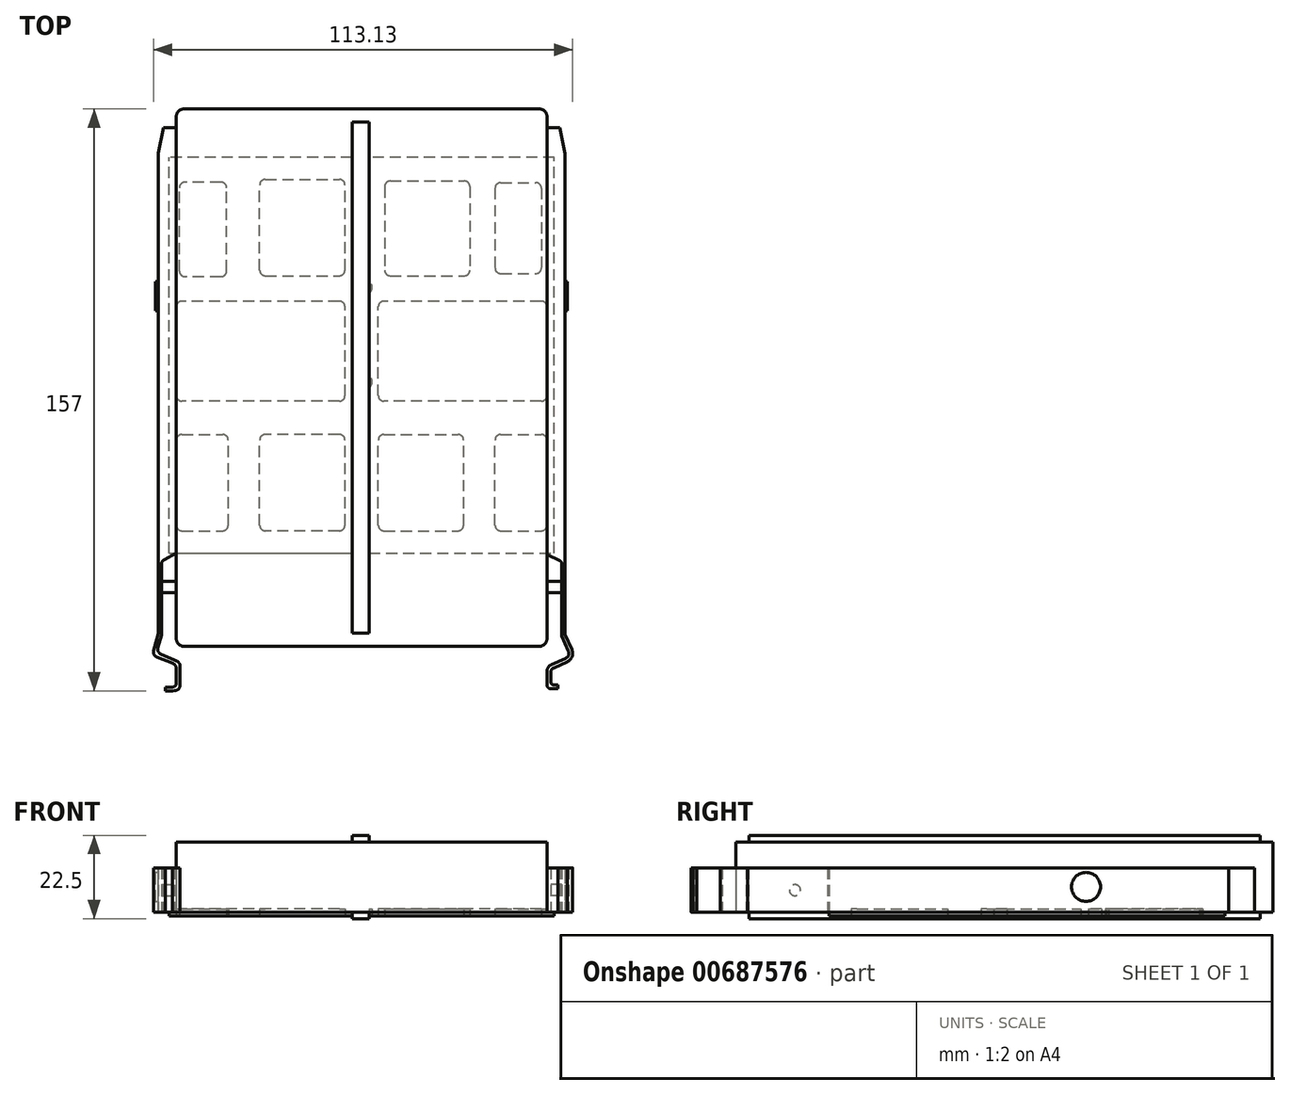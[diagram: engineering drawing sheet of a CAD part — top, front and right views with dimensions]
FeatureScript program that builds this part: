
annotation { "Feature Type Name" : "Feature", "Feature Type Description" : "" }
export const myFeature = defineFeature(function(context is Context, id is Id, definition is map)
    precondition{}
    {
        {
            var Q0;
            Q0=qCreatedBy(makeId("Top.planeOp"),FACE);
            var sketch = newSketch(context, id + "F0", { "sketchPlane" : qUnion([Q0])});
            skLineSegment(sketch, "E0", {"start": v(45.84, 65.9) * mm, "end": v(45.84, -75.1) * mm});
            skLineSegment(sketch, "E1", {"start": v(43.84, 67.9) * mm, "end": v(-52.16, 67.9) * mm});
            skLineSegment(sketch, "E2", {"start": v(-54.16, 65.9) * mm, "end": v(-54.16, -75.1) * mm});
            skLineSegment(sketch, "E3", {"start": v(-52.16, -77.1) * mm, "end": v(43.84, -77.1) * mm});
            skPoint(sketch, "E4.visualSharp", {"position": v(-54.16, 67.9) * mm});
            skArc(sketch, "E4.filletArc", {"start": v(-52.16, 67.9) * mm, "mid": v(-53.58, 67.31) * mm, "end": v(-54.16, 65.9) * mm});
            skPoint(sketch, "E5.visualSharp", {"position": v(45.84, 67.9) * mm});
            skArc(sketch, "E5.filletArc", {"start": v(45.84, 65.9) * mm, "mid": v(45.25, 67.31) * mm, "end": v(43.84, 67.9) * mm});
            skPoint(sketch, "E6.visualSharp", {"position": v(-54.16, -77.1) * mm});
            skArc(sketch, "E6.filletArc", {"start": v(-54.16, -75.1) * mm, "mid": v(-53.58, -76.52) * mm, "end": v(-52.16, -77.1) * mm});
            skPoint(sketch, "E7.visualSharp", {"position": v(45.84, -77.1) * mm});
            skArc(sketch, "E7.filletArc", {"start": v(43.84, -77.1) * mm, "mid": v(45.25, -76.52) * mm, "end": v(45.84, -75.1) * mm});
            skSolve(sketch);
        }
        {
            var Q0;
            Q0=makeQuery(id+"F0.imprint","IMPRINT",FACE,{"disambiguationData":[TD([[makeQuery(id+"F0.imprint","IMPRINT",EDGE,{"derivedFrom":sQuery(id+"F0.wireOp",EDGE,"E0")}),-1.0]])]});
            extrude(context, id + "F1", {"entities" : qUnion([Q0]), "depth" : 19 * mm, "offsetDistance" : 25 * mm});
        }
        {
            var Q0;
            Q0=makeQuery(id+"F1.opExtrude","SWEPT_FACE",FACE,{"disambiguationData":[OSD([sQuery(id+"F0.wireOp",EDGE,"E2")])]});
            var sketch = newSketch(context, id + "F2", { "sketchPlane" : qUnion([Q0])});
            skCircle(sketch, "E8", {"center": v(61.1, 6) * mm, "radius": 1.5 * mm});
            skSolve(sketch);
        }
        {
            var Q0;
            Q0=makeQuery(id+"F2.imprint","IMPRINT",FACE,{"disambiguationData":[TD([[makeQuery(id+"F2.imprint","IMPRINT",EDGE,{"derivedFrom":sQuery(id+"F2.wireOp",EDGE,"E8")}),1.0]])]});
            extrude(context, id + "F3", {"entities" : qUnion([Q0]), "operationType" : NewBodyOperationType.ADD, "depth" : 4 * mm, "offsetDistance" : 25 * mm});
        }
        {
            var Q0;
            Q0=makeQuery(id+"F1.opExtrude","SWEPT_FACE",FACE,{"disambiguationData":[OSD([sQuery(id+"F0.wireOp",EDGE,"E0")])]});
            var sketch = newSketch(context, id + "F4", { "sketchPlane" : qUnion([Q0])});
            skCircle(sketch, "E9", {"center": v(-61.1, 6) * mm, "radius": 1.5 * mm});
            skSolve(sketch);
        }
        {
            var Q0;
            Q0=makeQuery(id+"F4.imprint","IMPRINT",FACE,{"disambiguationData":[TD([[makeQuery(id+"F4.imprint","IMPRINT",EDGE,{"derivedFrom":sQuery(id+"F4.wireOp",EDGE,"E9")}),1.0]])]});
            extrude(context, id + "F5", {"entities" : qUnion([Q0]), "operationType" : NewBodyOperationType.ADD, "depth" : 4 * mm, "offsetDistance" : 25 * mm});
        }
        {
            var Q0;
            Q0=makeQuery(id+"F1.opExtrude","CAP_FACE",FACE,{"disambiguationData":[OSD([sQuery(id+"F0.wireOp",EDGE,"E0"),sQuery(id+"F0.wireOp",EDGE,"E1"),sQuery(id+"F0.wireOp",EDGE,"E2"),sQuery(id+"F0.wireOp",EDGE,"E3"),sQuery(id+"F0.wireOp",EDGE,"E4.filletArc"),sQuery(id+"F0.wireOp",EDGE,"E5.filletArc"),sQuery(id+"F0.wireOp",EDGE,"E6.filletArc"),sQuery(id+"F0.wireOp",EDGE,"E7.filletArc")])],"isStart":true});
            var sketch = newSketch(context, id + "F6", { "sketchPlane" : qUnion([Q0])});
            skLineSegment(sketch, "E10", {"start": v(46.84, 88.57) * mm, "end": v(48.84, 88.57) * mm});
            skLineSegment(sketch, "E11", {"start": v(45.84, 87.57) * mm, "end": v(45.84, 83.87) * mm});
            skPoint(sketch, "E12.visualSharp", {"position": v(45.84, 88.57) * mm});
            skArc(sketch, "E12.filletArc", {"start": v(46.84, 88.57) * mm, "mid": v(46.13, 88.28) * mm, "end": v(45.84, 87.57) * mm});
            skLineSegment(sketch, "E13", {"start": v(47.03, 82.04) * mm, "end": v(50.87, 80.36) * mm});
            skPoint(sketch, "E14.visualSharp", {"position": v(45.84, 82.57) * mm});
            skArc(sketch, "E14.filletArc", {"start": v(45.84, 83.87) * mm, "mid": v(46.16, 82.78) * mm, "end": v(47.03, 82.04) * mm});
            skLineSegment(sketch, "E15", {"start": v(51.64, 78.38) * mm, "end": v(49.84, 74.26) * mm});
            skPoint(sketch, "E16.visualSharp", {"position": v(52.25, 79.76) * mm});
            skArc(sketch, "E16.filletArc", {"start": v(51.64, 78.38) * mm, "mid": v(51.67, 79.53) * mm, "end": v(50.87, 80.36) * mm});
            skArc(sketch, "E17.filletArc", {"start": v(51.7, 79.44) * mm, "mid": v(51.7, 79.45) * mm, "end": v(51.68, 79.45) * mm});
            skPoint(sketch, "E18.end.orphan", {"position": v(53.66, 79.76) * mm});
            skLineSegment(sketch, "E19.0", {"start": v(52.56, 77.98) * mm, "end": v(50.75, 73.86) * mm});
            skArc(sketch, "E19.1", {"start": v(52.56, 77.98) * mm, "mid": v(52.6, 79.9) * mm, "end": v(51.27, 81.27) * mm});
            skLineSegment(sketch, "E20", {"start": v(48.84, 87.57) * mm, "end": v(48.84, 88.57) * mm});
            skLineSegment(sketch, "E21", {"start": v(48.84, 87.57) * mm, "end": v(47.84, 87.57) * mm});
            skLineSegment(sketch, "E22", {"start": v(46.84, 86.57) * mm, "end": v(46.84, 84.24) * mm});
            skArc(sketch, "E23.filletArc", {"start": v(47.84, 87.57) * mm, "mid": v(47.13, 87.28) * mm, "end": v(46.84, 86.57) * mm});
            skLineSegment(sketch, "E24", {"start": v(51.27, 81.27) * mm, "end": v(47.72, 82.88) * mm});
            skPoint(sketch, "E25.visualSharp", {"position": v(46.84, 83.27) * mm});
            skArc(sketch, "E25.filletArc", {"start": v(46.84, 84.24) * mm, "mid": v(47.08, 83.43) * mm, "end": v(47.72, 82.88) * mm});
            skLineSegment(sketch, "E26", {"start": v(49.84, 74.26) * mm, "end": v(49.84, 54.89) * mm});
            skLineSegment(sketch, "E27", {"start": v(50.75, 73.86) * mm, "end": v(50.75, -55.9) * mm});
            skLineSegment(sketch, "E28", {"start": v(49.25, -62.9) * mm, "end": v(45.84, -62.9) * mm});
            skLineSegment(sketch, "E29", {"start": v(49.25, -62.9) * mm, "end": v(50.75, -55.9) * mm});
            skPoint(sketch, "E30.orphan", {"position": v(50.75, -62.9) * mm});
            skLineSegment(sketch, "E31", {"start": v(49.27, 53.99) * mm, "end": v(45.84, 52.33) * mm});
            skPoint(sketch, "E32.visualSharp", {"position": v(49.84, 54.26) * mm});
            skArc(sketch, "E32.filletArc", {"start": v(49.27, 53.99) * mm, "mid": v(49.68, 54.36) * mm, "end": v(49.84, 54.89) * mm});
            skSolve(sketch);
        }
        {
            var Q0;
            Q0 = qSketchRegion(id + "F6", true);
            var Q1;
            Q1=makeQuery(id+"F6.imprint","IMPRINT",FACE,{"disambiguationData":[TD([[makeQuery(id+"F6.imprint","IMPRINT",EDGE,{"derivedFrom":sQuery(id+"F6.wireOp",EDGE,"E10")}),-1.0]])]});
            extrude(context, id + "F7", {"entities" : qUnion([Q0, Q1]), "oppositeDirection" : true, "depth" : 12 * mm, "offsetDistance" : 25 * mm});
        }
        {
            var Q0;
            Q0=makeQuery(id+"F1.opExtrude","CAP_FACE",FACE,{"disambiguationData":[OSD([sQuery(id+"F0.wireOp",EDGE,"E0"),sQuery(id+"F0.wireOp",EDGE,"E1"),sQuery(id+"F0.wireOp",EDGE,"E2"),sQuery(id+"F0.wireOp",EDGE,"E3"),sQuery(id+"F0.wireOp",EDGE,"E4.filletArc"),sQuery(id+"F0.wireOp",EDGE,"E5.filletArc"),sQuery(id+"F0.wireOp",EDGE,"E6.filletArc"),sQuery(id+"F0.wireOp",EDGE,"E7.filletArc")])],"isStart":true});
            var sketch = newSketch(context, id + "F8", { "sketchPlane" : qUnion([Q0])});
            skLineSegment(sketch, "E33", {"start": v(-57.58, -62.9) * mm, "end": v(-54.16, -62.9) * mm});
            skLineSegment(sketch, "E34", {"start": v(-57.58, -62.9) * mm, "end": v(-59.08, -56.06) * mm});
            skLineSegment(sketch, "E35", {"start": v(-59.08, -56.06) * mm, "end": v(-59.08, 73.7) * mm});
            skPoint(sketch, "E36.visualSharp", {"position": v(-58.08, 53.7) * mm});
            skLineSegment(sketch, "E37", {"start": v(-58.16, 74.1) * mm, "end": v(-58.16, 55) * mm});
            skLineSegment(sketch, "E38", {"start": v(-57.38, 53.67) * mm, "end": v(-54.16, 51.94) * mm});
            skPoint(sketch, "E39.visualSharp", {"position": v(-58.16, 54.1) * mm});
            skArc(sketch, "E39.filletArc", {"start": v(-58.16, 55) * mm, "mid": v(-57.95, 54.23) * mm, "end": v(-57.38, 53.67) * mm});
            skLineSegment(sketch, "E40", {"start": v(-55.16, 88.1) * mm, "end": v(-57.16, 88.1) * mm});
            skLineSegment(sketch, "E41", {"start": v(-54.16, 87.1) * mm, "end": v(-54.16, 83.11) * mm});
            skPoint(sketch, "E42.visualSharp", {"position": v(-54.16, 88.1) * mm});
            skArc(sketch, "E42.filletArc", {"start": v(-54.16, 87.1) * mm, "mid": v(-54.46, 87.8) * mm, "end": v(-55.16, 88.1) * mm});
            skLineSegment(sketch, "E43", {"start": v(-55.1, 81.72) * mm, "end": v(-59.42, 79.99) * mm});
            skPoint(sketch, "E44.visualSharp", {"position": v(-54.16, 82.1) * mm});
            skArc(sketch, "E44.filletArc", {"start": v(-55.1, 81.72) * mm, "mid": v(-54.42, 82.27) * mm, "end": v(-54.16, 83.11) * mm});
            skLineSegment(sketch, "E45", {"start": v(-60.3, 78.2) * mm, "end": v(-59.08, 73.7) * mm});
            skPoint(sketch, "E46.visualSharp", {"position": v(-60.66, 79.49) * mm});
            skArc(sketch, "E46.filletArc", {"start": v(-59.42, 79.99) * mm, "mid": v(-60.2, 79.26) * mm, "end": v(-60.3, 78.2) * mm});
            skLineSegment(sketch, "E47", {"start": v(-58.16, 74.1) * mm, "end": v(-59.1, 77.52) * mm});
            skLineSegment(sketch, "E48.0", {"start": v(-53.16, 87.1) * mm, "end": v(-53.16, 83.11) * mm});
            skLineSegment(sketch, "E49", {"start": v(-54.73, 80.8) * mm, "end": v(-54.18, 80.98) * mm});
            skLineSegment(sketch, "E50", {"start": v(-53.16, 82.4) * mm, "end": v(-53.16, 83.11) * mm});
            skPoint(sketch, "E51.visualSharp", {"position": v(-53.16, 81.33) * mm});
            skArc(sketch, "E51.filletArc", {"start": v(-54.18, 80.98) * mm, "mid": v(-53.44, 81.53) * mm, "end": v(-53.16, 82.4) * mm});
            skLineSegment(sketch, "E52", {"start": v(-57.16, 88.1) * mm, "end": v(-57.16, 89.1) * mm});
            skLineSegment(sketch, "E53.0", {"start": v(-55.16, 89.1) * mm, "end": v(-57.16, 89.1) * mm});
            skLineSegment(sketch, "E54", {"start": v(-53.16, 87.1) * mm, "end": v(-53.16, 87.6) * mm});
            skLineSegment(sketch, "E55", {"start": v(-54.65, 89.1) * mm, "end": v(-55.16, 89.1) * mm});
            skPoint(sketch, "E56.visualSharp", {"position": v(-53.16, 89.08) * mm});
            skArc(sketch, "E56.filletArc", {"start": v(-53.16, 87.6) * mm, "mid": v(-53.6, 88.65) * mm, "end": v(-54.65, 89.1) * mm});
            skLineSegment(sketch, "E57", {"start": v(-54.16, -62.9) * mm, "end": v(-54.16, 51.94) * mm});
            skLineSegment(sketch, "E58", {"start": v(-58.24, 79.3) * mm, "end": v(-54.73, 80.8) * mm});
            skPoint(sketch, "E59.visualSharp", {"position": v(-59.44, 78.78) * mm});
            skArc(sketch, "E59.filletArc", {"start": v(-58.24, 79.3) * mm, "mid": v(-59, 78.57) * mm, "end": v(-59.1, 77.52) * mm});
            skSolve(sketch);
        }
        {
            var Q0;
            Q0 = qSketchRegion(id + "F8", true);
            extrude(context, id + "F9", {"entities" : qUnion([Q0]), "oppositeDirection" : true, "depth" : 12 * mm, "offsetDistance" : 25 * mm});
        }
        {
            var Q0;
            Q0=makeQuery(id+"F1.opExtrude","CAP_FACE",FACE,{"disambiguationData":[OSD([sQuery(id+"F0.wireOp",EDGE,"E0"),sQuery(id+"F0.wireOp",EDGE,"E1"),sQuery(id+"F0.wireOp",EDGE,"E2"),sQuery(id+"F0.wireOp",EDGE,"E3"),sQuery(id+"F0.wireOp",EDGE,"E4.filletArc"),sQuery(id+"F0.wireOp",EDGE,"E5.filletArc"),sQuery(id+"F0.wireOp",EDGE,"E6.filletArc"),sQuery(id+"F0.wireOp",EDGE,"E7.filletArc")])],"isStart":true});
            var sketch = newSketch(context, id + "F10", { "sketchPlane" : qUnion([Q0])});
            skLineSegment(sketch, "E60", {"start": v(-54.16, 51.94) * mm, "end": v(-56.16, 51.94) * mm});
            skLineSegment(sketch, "E61", {"start": v(45.84, 51.94) * mm, "end": v(47.84, 51.94) * mm});
            skLineSegment(sketch, "E62.left", {"start": v(47.84, 51.94) * mm, "end": v(47.84, 51.94) * mm});
            skLineSegment(sketch, "E62.right", {"start": v(-56.16, 51.94) * mm, "end": v(-56.16, 51.94) * mm});
            skLineSegment(sketch, "E63.bottom", {"start": v(47.84, 51.94) * mm, "end": v(-56.16, 51.94) * mm});
            skLineSegment(sketch, "E63.top", {"start": v(47.84, -54.9) * mm, "end": v(-56.16, -54.9) * mm});
            skLineSegment(sketch, "E63.left", {"start": v(47.84, 51.94) * mm, "end": v(47.84, -54.9) * mm});
            skLineSegment(sketch, "E63.right", {"start": v(-56.16, 51.94) * mm, "end": v(-56.16, -54.9) * mm});
            skSolve(sketch);
        }
        {
            var Q0;
            {var subQ0=sQuery(id+"F10.wireOp",EDGE,"E63.left");Q0=makeQuery(id+"F10.imprint","IMPRINT",FACE,{"disambiguationData":[TD([[makeQuery(id+"F10.imprint","IMPRINT",EDGE,{"derivedFrom":subQ0}),-1.0]])]});}
            var Q1;
            {var subQ0=sQuery(id+"F10.wireOp",EDGE,"E63.right");Q1=makeQuery(id+"F10.imprint","IMPRINT",FACE,{"disambiguationData":[TD([[makeQuery(id+"F10.imprint","IMPRINT",EDGE,{"derivedFrom":subQ0}),1.0]])]});}
            var Q2;
            {var subQ0=sQuery(id+"F10.wireOp",EDGE,"E63.bottom");var subQ1=makeQuery(id+"F1.opExtrude","CAP_EDGE",EDGE,{"disambiguationData":[OSD([sQuery(id+"F0.wireOp",EDGE,"E2")])],"isStart":true});var subQ2=makeQuery(id+"F10.imprint","INTERSECT",VERTEX,{"derivedFrom":[subQ1,subQ0]});Q2=makeQuery(id+"F10.imprint","IMPRINT",FACE,{"disambiguationData":[TD([[makeQuery(id+"F10.imprint","IMPRINT",EDGE,{"disambiguationData":[TD([[subQ2,1.0]])],"derivedFrom":subQ0}),1.0]])]});}
            extrude(context, id + "F11", {"entities" : qUnion([Q0, Q1, Q2]), "depth" : 1 * mm, "offsetDistance" : 25 * mm});
        }
        {
            var Q0;
            Q0=makeQuery(id+"F11.opExtrude","CAP_FACE",FACE,{"disambiguationData":[OSD([sQuery(id+"F10.wireOp",EDGE,"E63.bottom"),sQuery(id+"F10.wireOp",EDGE,"E63.top"),sQuery(id+"F10.wireOp",EDGE,"E63.left"),sQuery(id+"F10.wireOp",EDGE,"E63.right")])],"isStart":false});
            var sketch = newSketch(context, id + "F12", { "sketchPlane" : qUnion([Q0])});
            skLineSegment(sketch, "E64.bottom", {"start": v(-52.66, 45.94) * mm, "end": v(-41.66, 45.94) * mm});
            skLineSegment(sketch, "E64.top", {"start": v(-52.66, 19.94) * mm, "end": v(-41.66, 19.94) * mm});
            skLineSegment(sketch, "E64.left", {"start": v(-54.16, 44.44) * mm, "end": v(-54.16, 21.44) * mm});
            skLineSegment(sketch, "E64.right", {"start": v(-40.16, 44.44) * mm, "end": v(-40.16, 21.44) * mm});
            skPoint(sketch, "E65.visualSharp", {"position": v(-54.16, 45.94) * mm});
            skArc(sketch, "E65.filletArc", {"start": v(-52.66, 45.94) * mm, "mid": v(-53.72, 45.5) * mm, "end": v(-54.16, 44.44) * mm});
            skPoint(sketch, "E66.visualSharp", {"position": v(-54.16, 19.94) * mm});
            skArc(sketch, "E66.filletArc", {"start": v(-54.16, 21.44) * mm, "mid": v(-53.72, 20.38) * mm, "end": v(-52.66, 19.94) * mm});
            skPoint(sketch, "E67.visualSharp", {"position": v(-40.16, 19.94) * mm});
            skArc(sketch, "E67.filletArc", {"start": v(-41.66, 19.94) * mm, "mid": v(-40.6, 20.38) * mm, "end": v(-40.16, 21.44) * mm});
            skPoint(sketch, "E68.visualSharp", {"position": v(-40.16, 45.94) * mm});
            skArc(sketch, "E68.filletArc", {"start": v(-40.16, 44.44) * mm, "mid": v(-40.6, 45.5) * mm, "end": v(-41.66, 45.94) * mm});
            skSolve(sketch);
        }
        {
            var Q0;
            Q0=makeQuery(id+"F12.imprint","IMPRINT",FACE,{"disambiguationData":[TD([[makeQuery(id+"F12.imprint","IMPRINT",EDGE,{"derivedFrom":sQuery(id+"F12.wireOp",EDGE,"E64.bottom")}),-1.0]])]});
            extrude(context, id + "F13", {"entities" : qUnion([Q0]), "operationType" : NewBodyOperationType.REMOVE, "oppositeDirection" : true, "depth" : 2 * mm, "offsetDistance" : 25 * mm});
        }
        {
            var Q0;
            Q0=makeQuery(id+"F11.opExtrude","CAP_FACE",FACE,{"disambiguationData":[OSD([sQuery(id+"F10.wireOp",EDGE,"E63.bottom"),sQuery(id+"F10.wireOp",EDGE,"E63.top"),sQuery(id+"F10.wireOp",EDGE,"E63.left"),sQuery(id+"F10.wireOp",EDGE,"E63.right")])],"isStart":false});
            var sketch = newSketch(context, id + "F14", { "sketchPlane" : qUnion([Q0])});
            skLineSegment(sketch, "E69.bottom", {"start": v(-10.16, 45.94) * mm, "end": v(-30.16, 45.94) * mm});
            skLineSegment(sketch, "E69.top", {"start": v(-10.16, 19.94) * mm, "end": v(-30.16, 19.94) * mm});
            skLineSegment(sketch, "E69.left", {"start": v(-8.66, 44.44) * mm, "end": v(-8.66, 21.44) * mm});
            skLineSegment(sketch, "E69.right", {"start": v(-31.66, 44.44) * mm, "end": v(-31.66, 21.44) * mm});
            skPoint(sketch, "E70.visualSharp", {"position": v(-31.66, 45.94) * mm});
            skArc(sketch, "E70.filletArc", {"start": v(-30.16, 45.94) * mm, "mid": v(-31.22, 45.5) * mm, "end": v(-31.66, 44.44) * mm});
            skPoint(sketch, "E71.visualSharp", {"position": v(-31.66, 19.94) * mm});
            skArc(sketch, "E71.filletArc", {"start": v(-31.66, 21.44) * mm, "mid": v(-31.22, 20.38) * mm, "end": v(-30.16, 19.94) * mm});
            skPoint(sketch, "E72.visualSharp", {"position": v(-8.66, 19.94) * mm});
            skArc(sketch, "E72.filletArc", {"start": v(-10.16, 19.94) * mm, "mid": v(-9.1, 20.38) * mm, "end": v(-8.66, 21.44) * mm});
            skPoint(sketch, "E73.visualSharp", {"position": v(-8.66, 45.94) * mm});
            skArc(sketch, "E73.filletArc", {"start": v(-8.66, 44.44) * mm, "mid": v(-9.1, 45.5) * mm, "end": v(-10.16, 45.94) * mm});
            skSolve(sketch);
        }
        {
            var Q0;
            Q0=makeQuery(id+"F14.imprint","IMPRINT",FACE,{"disambiguationData":[TD([[makeQuery(id+"F14.imprint","IMPRINT",EDGE,{"derivedFrom":sQuery(id+"F14.wireOp",EDGE,"E69.bottom")}),1.0]])]});
            extrude(context, id + "F15", {"entities" : qUnion([Q0]), "operationType" : NewBodyOperationType.REMOVE, "oppositeDirection" : true, "depth" : 2 * mm, "offsetDistance" : 25 * mm});
        }
        {
            var Q0;
            Q0=makeQuery(id+"F11.opExtrude","CAP_FACE",FACE,{"disambiguationData":[OSD([sQuery(id+"F10.wireOp",EDGE,"E63.bottom"),sQuery(id+"F10.wireOp",EDGE,"E63.top"),sQuery(id+"F10.wireOp",EDGE,"E63.left"),sQuery(id+"F10.wireOp",EDGE,"E63.right")])],"isStart":false});
            var sketch = newSketch(context, id + "F16", { "sketchPlane" : qUnion([Q0])});
            skLineSegment(sketch, "E74.bottom", {"start": v(1.84, 45.94) * mm, "end": v(21.84, 45.94) * mm});
            skLineSegment(sketch, "E74.top", {"start": v(1.84, 19.94) * mm, "end": v(21.84, 19.94) * mm});
            skLineSegment(sketch, "E74.left", {"start": v(0.34, 44.44) * mm, "end": v(0.34, 21.44) * mm});
            skLineSegment(sketch, "E74.right", {"start": v(23.34, 44.44) * mm, "end": v(23.34, 21.44) * mm});
            skPoint(sketch, "E75.visualSharp", {"position": v(0.34, 45.94) * mm});
            skArc(sketch, "E75.filletArc", {"start": v(1.84, 45.94) * mm, "mid": v(0.78, 45.5) * mm, "end": v(0.34, 44.44) * mm});
            skPoint(sketch, "E76.visualSharp", {"position": v(23.34, 45.94) * mm});
            skArc(sketch, "E76.filletArc", {"start": v(23.34, 44.44) * mm, "mid": v(22.9, 45.5) * mm, "end": v(21.84, 45.94) * mm});
            skPoint(sketch, "E77.visualSharp", {"position": v(23.34, 19.94) * mm});
            skArc(sketch, "E77.filletArc", {"start": v(21.84, 19.94) * mm, "mid": v(22.9, 20.38) * mm, "end": v(23.34, 21.44) * mm});
            skPoint(sketch, "E78.visualSharp", {"position": v(0.34, 19.94) * mm});
            skArc(sketch, "E78.filletArc", {"start": v(0.34, 21.44) * mm, "mid": v(0.78, 20.38) * mm, "end": v(1.84, 19.94) * mm});
            skSolve(sketch);
        }
        {
            var Q0;
            Q0=makeQuery(id+"F16.imprint","IMPRINT",FACE,{"disambiguationData":[TD([[makeQuery(id+"F16.imprint","IMPRINT",EDGE,{"derivedFrom":sQuery(id+"F16.wireOp",EDGE,"E74.bottom")}),-1.0]])]});
            extrude(context, id + "F17", {"entities" : qUnion([Q0]), "operationType" : NewBodyOperationType.REMOVE, "oppositeDirection" : true, "depth" : 2 * mm, "offsetDistance" : 25 * mm});
        }
        {
            var Q0;
            Q0=makeQuery(id+"F11.opExtrude","CAP_FACE",FACE,{"disambiguationData":[OSD([sQuery(id+"F10.wireOp",EDGE,"E63.bottom"),sQuery(id+"F10.wireOp",EDGE,"E63.top"),sQuery(id+"F10.wireOp",EDGE,"E63.left"),sQuery(id+"F10.wireOp",EDGE,"E63.right")])],"isStart":false});
            var sketch = newSketch(context, id + "F18", { "sketchPlane" : qUnion([Q0])});
            skLineSegment(sketch, "E79.bottom", {"start": v(33.34, 45.94) * mm, "end": v(44.34, 45.94) * mm});
            skLineSegment(sketch, "E79.top", {"start": v(33.34, 19.94) * mm, "end": v(44.34, 19.94) * mm});
            skLineSegment(sketch, "E79.left", {"start": v(31.84, 44.44) * mm, "end": v(31.84, 21.44) * mm});
            skLineSegment(sketch, "E79.right", {"start": v(45.84, 44.44) * mm, "end": v(45.84, 21.44) * mm});
            skPoint(sketch, "E80.visualSharp", {"position": v(31.84, 45.94) * mm});
            skArc(sketch, "E80.filletArc", {"start": v(33.34, 45.94) * mm, "mid": v(32.28, 45.5) * mm, "end": v(31.84, 44.44) * mm});
            skPoint(sketch, "E81.visualSharp", {"position": v(31.84, 19.94) * mm});
            skArc(sketch, "E81.filletArc", {"start": v(31.84, 21.44) * mm, "mid": v(32.28, 20.38) * mm, "end": v(33.34, 19.94) * mm});
            skPoint(sketch, "E82.visualSharp", {"position": v(45.84, 19.94) * mm});
            skArc(sketch, "E82.filletArc", {"start": v(44.34, 19.94) * mm, "mid": v(45.4, 20.38) * mm, "end": v(45.84, 21.44) * mm});
            skPoint(sketch, "E83.visualSharp", {"position": v(45.84, 45.94) * mm});
            skArc(sketch, "E83.filletArc", {"start": v(45.84, 44.44) * mm, "mid": v(45.4, 45.5) * mm, "end": v(44.34, 45.94) * mm});
            skSolve(sketch);
        }
        {
            var Q0;
            Q0=makeQuery(id+"F18.imprint","IMPRINT",FACE,{"disambiguationData":[TD([[makeQuery(id+"F18.imprint","IMPRINT",EDGE,{"derivedFrom":sQuery(id+"F18.wireOp",EDGE,"E79.bottom")}),-1.0]])]});
            extrude(context, id + "F19", {"entities" : qUnion([Q0]), "operationType" : NewBodyOperationType.REMOVE, "oppositeDirection" : true, "depth" : 2 * mm, "offsetDistance" : 25 * mm});
        }
        {
            var Q0;
            Q0=makeQuery(id+"F11.opExtrude","CAP_FACE",FACE,{"disambiguationData":[OSD([sQuery(id+"F10.wireOp",EDGE,"E63.bottom"),sQuery(id+"F10.wireOp",EDGE,"E63.top"),sQuery(id+"F10.wireOp",EDGE,"E63.left"),sQuery(id+"F10.wireOp",EDGE,"E63.right")])],"isStart":false});
            var sketch = newSketch(context, id + "F20", { "sketchPlane" : qUnion([Q0])});
            skLineSegment(sketch, "E84.bottom", {"start": v(44.34, 10.94) * mm, "end": v(1.84, 10.94) * mm});
            skLineSegment(sketch, "E84.top", {"start": v(44.34, -16.06) * mm, "end": v(1.84, -16.06) * mm});
            skLineSegment(sketch, "E84.left", {"start": v(45.84, 9.44) * mm, "end": v(45.84, -14.56) * mm});
            skLineSegment(sketch, "E84.right", {"start": v(0.34, 9.44) * mm, "end": v(0.34, -14.56) * mm});
            skPoint(sketch, "E85.visualSharp", {"position": v(0.34, 10.94) * mm});
            skArc(sketch, "E85.filletArc", {"start": v(1.84, 10.94) * mm, "mid": v(0.78, 10.5) * mm, "end": v(0.34, 9.44) * mm});
            skPoint(sketch, "E86.visualSharp", {"position": v(45.84, 10.94) * mm});
            skArc(sketch, "E86.filletArc", {"start": v(45.84, 9.44) * mm, "mid": v(45.4, 10.5) * mm, "end": v(44.34, 10.94) * mm});
            skPoint(sketch, "E87.visualSharp", {"position": v(45.84, -16.06) * mm});
            skArc(sketch, "E87.filletArc", {"start": v(44.34, -16.06) * mm, "mid": v(45.4, -15.62) * mm, "end": v(45.84, -14.56) * mm});
            skPoint(sketch, "E88.visualSharp", {"position": v(0.34, -16.06) * mm});
            skArc(sketch, "E88.filletArc", {"start": v(0.34, -14.56) * mm, "mid": v(0.78, -15.62) * mm, "end": v(1.84, -16.06) * mm});
            skSolve(sketch);
        }
        {
            var Q0;
            Q0=makeQuery(id+"F20.imprint","IMPRINT",FACE,{"disambiguationData":[TD([[makeQuery(id+"F20.imprint","IMPRINT",EDGE,{"derivedFrom":sQuery(id+"F20.wireOp",EDGE,"E84.bottom")}),1.0]])]});
            extrude(context, id + "F21", {"entities" : qUnion([Q0]), "operationType" : NewBodyOperationType.REMOVE, "oppositeDirection" : true, "depth" : 2 * mm, "offsetDistance" : 25 * mm});
        }
        {
            var Q0;
            Q0=makeQuery(id+"F11.opExtrude","CAP_FACE",FACE,{"disambiguationData":[OSD([sQuery(id+"F10.wireOp",EDGE,"E63.bottom"),sQuery(id+"F10.wireOp",EDGE,"E63.top"),sQuery(id+"F10.wireOp",EDGE,"E63.left"),sQuery(id+"F10.wireOp",EDGE,"E63.right")])],"isStart":false});
            var sketch = newSketch(context, id + "F22", { "sketchPlane" : qUnion([Q0])});
            skLineSegment(sketch, "E89.bottom", {"start": v(-10.16, 10.94) * mm, "end": v(-52.66, 10.94) * mm});
            skLineSegment(sketch, "E89.top", {"start": v(-10.16, -16.06) * mm, "end": v(-52.66, -16.06) * mm});
            skLineSegment(sketch, "E89.left", {"start": v(-8.66, 9.44) * mm, "end": v(-8.66, -14.56) * mm});
            skLineSegment(sketch, "E89.right", {"start": v(-54.16, 9.44) * mm, "end": v(-54.16, -14.56) * mm});
            skPoint(sketch, "E90.visualSharp", {"position": v(-54.16, 10.94) * mm});
            skArc(sketch, "E90.filletArc", {"start": v(-52.66, 10.94) * mm, "mid": v(-53.72, 10.5) * mm, "end": v(-54.16, 9.44) * mm});
            skPoint(sketch, "E91.visualSharp", {"position": v(-54.16, -16.06) * mm});
            skArc(sketch, "E91.filletArc", {"start": v(-54.16, -14.56) * mm, "mid": v(-53.72, -15.62) * mm, "end": v(-52.66, -16.06) * mm});
            skPoint(sketch, "E92.visualSharp", {"position": v(-8.66, -16.06) * mm});
            skArc(sketch, "E92.filletArc", {"start": v(-10.16, -16.06) * mm, "mid": v(-9.1, -15.62) * mm, "end": v(-8.66, -14.56) * mm});
            skPoint(sketch, "E93.visualSharp", {"position": v(-8.66, 10.94) * mm});
            skArc(sketch, "E93.filletArc", {"start": v(-8.66, 9.44) * mm, "mid": v(-9.1, 10.5) * mm, "end": v(-10.16, 10.94) * mm});
            skSolve(sketch);
        }
        {
            var Q0;
            Q0=makeQuery(id+"F22.imprint","IMPRINT",FACE,{"disambiguationData":[TD([[makeQuery(id+"F22.imprint","IMPRINT",EDGE,{"derivedFrom":sQuery(id+"F22.wireOp",EDGE,"E89.bottom")}),1.0]])]});
            extrude(context, id + "F23", {"entities" : qUnion([Q0]), "operationType" : NewBodyOperationType.REMOVE, "oppositeDirection" : true, "depth" : 2 * mm, "offsetDistance" : 25 * mm});
        }
        {
            var Q0;
            Q0=makeQuery(id+"F11.opExtrude","CAP_FACE",FACE,{"disambiguationData":[OSD([sQuery(id+"F10.wireOp",EDGE,"E63.bottom"),sQuery(id+"F10.wireOp",EDGE,"E63.top"),sQuery(id+"F10.wireOp",EDGE,"E63.left"),sQuery(id+"F10.wireOp",EDGE,"E63.right")])],"isStart":false});
            var sketch = newSketch(context, id + "F24", { "sketchPlane" : qUnion([Q0])});
            skLineSegment(sketch, "E94.bottom", {"start": v(-30.16, -22.9) * mm, "end": v(-10.16, -22.9) * mm});
            skLineSegment(sketch, "E94.top", {"start": v(-30.16, -48.9) * mm, "end": v(-10.16, -48.9) * mm});
            skLineSegment(sketch, "E94.left", {"start": v(-31.66, -24.4) * mm, "end": v(-31.66, -47.4) * mm});
            skLineSegment(sketch, "E94.right", {"start": v(-8.66, -24.4) * mm, "end": v(-8.66, -47.4) * mm});
            skPoint(sketch, "E95.visualSharp", {"position": v(-8.66, -48.9) * mm});
            skArc(sketch, "E95.filletArc", {"start": v(-10.16, -48.9) * mm, "mid": v(-9.1, -48.46) * mm, "end": v(-8.66, -47.4) * mm});
            skPoint(sketch, "E96.visualSharp", {"position": v(-31.66, -48.9) * mm});
            skArc(sketch, "E96.filletArc", {"start": v(-31.66, -47.4) * mm, "mid": v(-31.22, -48.46) * mm, "end": v(-30.16, -48.9) * mm});
            skPoint(sketch, "E97.visualSharp", {"position": v(-8.66, -22.9) * mm});
            skArc(sketch, "E97.filletArc", {"start": v(-8.66, -24.4) * mm, "mid": v(-9.1, -23.34) * mm, "end": v(-10.16, -22.9) * mm});
            skPoint(sketch, "E98.visualSharp", {"position": v(-31.66, -22.9) * mm});
            skArc(sketch, "E98.filletArc", {"start": v(-30.16, -22.9) * mm, "mid": v(-31.22, -23.34) * mm, "end": v(-31.66, -24.4) * mm});
            skSolve(sketch);
        }
        {
            var Q0;
            Q0=makeQuery(id+"F24.imprint","IMPRINT",FACE,{"disambiguationData":[TD([[makeQuery(id+"F24.imprint","IMPRINT",EDGE,{"derivedFrom":sQuery(id+"F24.wireOp",EDGE,"E94.bottom")}),-1.0]])]});
            extrude(context, id + "F25", {"entities" : qUnion([Q0]), "operationType" : NewBodyOperationType.REMOVE, "oppositeDirection" : true, "depth" : 2 * mm, "offsetDistance" : 25 * mm});
        }
        {
            var Q0;
            Q0=makeQuery(id+"F11.opExtrude","CAP_FACE",FACE,{"disambiguationData":[OSD([sQuery(id+"F10.wireOp",EDGE,"E63.bottom"),sQuery(id+"F10.wireOp",EDGE,"E63.top"),sQuery(id+"F10.wireOp",EDGE,"E63.left"),sQuery(id+"F10.wireOp",EDGE,"E63.right")])],"isStart":false});
            var sketch = newSketch(context, id + "F26", { "sketchPlane" : qUnion([Q0])});
            skPoint(sketch, "E99.firstSnap0", {"position": v(-9.1, -48.46) * mm});
            skLineSegment(sketch, "E99.bottom", {"start": v(3.55, -48.46) * mm, "end": v(23.55, -48.46) * mm});
            skLineSegment(sketch, "E99.top", {"start": v(3.55, -22.9) * mm, "end": v(23.55, -22.9) * mm});
            skLineSegment(sketch, "E99.left", {"start": v(2.05, -46.96) * mm, "end": v(2.05, -24.4) * mm});
            skLineSegment(sketch, "E99.right", {"start": v(25.05, -46.96) * mm, "end": v(25.05, -24.4) * mm});
            skPoint(sketch, "E100.visualSharp", {"position": v(2.05, -22.9) * mm});
            skArc(sketch, "E100.filletArc", {"start": v(3.55, -22.9) * mm, "mid": v(2.49, -23.34) * mm, "end": v(2.05, -24.4) * mm});
            skPoint(sketch, "E101.visualSharp", {"position": v(25.05, -22.9) * mm});
            skArc(sketch, "E101.filletArc", {"start": v(25.05, -24.4) * mm, "mid": v(24.6, -23.34) * mm, "end": v(23.55, -22.9) * mm});
            skPoint(sketch, "E102.visualSharp", {"position": v(2.05, -48.46) * mm});
            skArc(sketch, "E102.filletArc", {"start": v(2.05, -46.96) * mm, "mid": v(2.49, -48.02) * mm, "end": v(3.55, -48.46) * mm});
            skPoint(sketch, "E103.visualSharp", {"position": v(25.05, -48.46) * mm});
            skArc(sketch, "E103.filletArc", {"start": v(23.55, -48.46) * mm, "mid": v(24.6, -48.02) * mm, "end": v(25.05, -46.96) * mm});
            skSolve(sketch);
        }
        {
            var Q0;
            Q0 = qSketchRegion(id + "F26", true);
            extrude(context, id + "F27", {"entities" : qUnion([Q0]), "operationType" : NewBodyOperationType.REMOVE, "oppositeDirection" : true, "depth" : 2 * mm, "offsetDistance" : 25 * mm});
        }
        {
            var Q0;
            Q0=makeQuery(id+"F11.opExtrude","CAP_FACE",FACE,{"disambiguationData":[OSD([sQuery(id+"F10.wireOp",EDGE,"E63.bottom"),sQuery(id+"F10.wireOp",EDGE,"E63.top"),sQuery(id+"F10.wireOp",EDGE,"E63.left"),sQuery(id+"F10.wireOp",EDGE,"E63.right")])],"isStart":false});
            var sketch = newSketch(context, id + "F28", { "sketchPlane" : qUnion([Q0])});
            skPoint(sketch, "E104.firstSnap0", {"position": v(-40.6, 20.38) * mm});
            skLineSegment(sketch, "E104.bottom", {"start": v(-42.1, -22.66) * mm, "end": v(-51.83, -22.66) * mm});
            skLineSegment(sketch, "E104.top", {"start": v(-42.1, -48.13) * mm, "end": v(-51.83, -48.13) * mm});
            skLineSegment(sketch, "E104.left", {"start": v(-40.6, -24.16) * mm, "end": v(-40.6, -46.63) * mm});
            skLineSegment(sketch, "E104.right", {"start": v(-53.33, -24.16) * mm, "end": v(-53.33, -46.63) * mm});
            skPoint(sketch, "E105.visualSharp", {"position": v(-40.6, -48.13) * mm});
            skArc(sketch, "E105.filletArc", {"start": v(-42.1, -48.13) * mm, "mid": v(-41.04, -47.69) * mm, "end": v(-40.6, -46.63) * mm});
            skPoint(sketch, "E106.visualSharp", {"position": v(-53.33, -48.13) * mm});
            skArc(sketch, "E106.filletArc", {"start": v(-53.33, -46.63) * mm, "mid": v(-52.9, -47.69) * mm, "end": v(-51.83, -48.13) * mm});
            skPoint(sketch, "E107.visualSharp", {"position": v(-53.33, -22.66) * mm});
            skArc(sketch, "E107.filletArc", {"start": v(-51.83, -22.66) * mm, "mid": v(-52.9, -23.1) * mm, "end": v(-53.33, -24.16) * mm});
            skPoint(sketch, "E108.visualSharp", {"position": v(-40.6, -22.66) * mm});
            skArc(sketch, "E108.filletArc", {"start": v(-40.6, -24.16) * mm, "mid": v(-41.04, -23.1) * mm, "end": v(-42.1, -22.66) * mm});
            skSolve(sketch);
        }
        {
            var Q0;
            Q0 = qSketchRegion(id + "F28", true);
            extrude(context, id + "F29", {"entities" : qUnion([Q0]), "operationType" : NewBodyOperationType.REMOVE, "oppositeDirection" : true, "depth" : 2 * mm, "offsetDistance" : 25 * mm});
        }
        {
            var Q0;
            Q0=makeQuery(id+"F11.opExtrude","CAP_FACE",FACE,{"disambiguationData":[OSD([sQuery(id+"F10.wireOp",EDGE,"E63.bottom"),sQuery(id+"F10.wireOp",EDGE,"E63.top"),sQuery(id+"F10.wireOp",EDGE,"E63.left"),sQuery(id+"F10.wireOp",EDGE,"E63.right")])],"isStart":false});
            var sketch = newSketch(context, id + "F30", { "sketchPlane" : qUnion([Q0])});
            skPoint(sketch, "E109.firstSnap0", {"position": v(24.6, -48.02) * mm});
            skLineSegment(sketch, "E109.bottom", {"start": v(33.34, -48.02) * mm, "end": v(42.84, -48.02) * mm});
            skLineSegment(sketch, "E109.top", {"start": v(33.34, -23.5) * mm, "end": v(42.84, -23.5) * mm});
            skLineSegment(sketch, "E109.left", {"start": v(31.84, -46.52) * mm, "end": v(31.84, -25) * mm});
            skLineSegment(sketch, "E109.right", {"start": v(44.34, -46.52) * mm, "end": v(44.34, -25) * mm});
            skPoint(sketch, "E110.visualSharp", {"position": v(44.34, -48.02) * mm});
            skArc(sketch, "E110.filletArc", {"start": v(42.84, -48.02) * mm, "mid": v(43.9, -47.58) * mm, "end": v(44.34, -46.52) * mm});
            skPoint(sketch, "E111.visualSharp", {"position": v(31.84, -48.02) * mm});
            skArc(sketch, "E111.filletArc", {"start": v(31.84, -46.52) * mm, "mid": v(32.28, -47.58) * mm, "end": v(33.34, -48.02) * mm});
            skPoint(sketch, "E112.visualSharp", {"position": v(31.84, -23.5) * mm});
            skArc(sketch, "E112.filletArc", {"start": v(33.34, -23.5) * mm, "mid": v(32.28, -23.93) * mm, "end": v(31.84, -25) * mm});
            skPoint(sketch, "E113.visualSharp", {"position": v(44.34, -23.5) * mm});
            skArc(sketch, "E113.filletArc", {"start": v(44.34, -25) * mm, "mid": v(43.9, -23.93) * mm, "end": v(42.84, -23.5) * mm});
            skSolve(sketch);
        }
        {
            var Q0;
            Q0 = qSketchRegion(id + "F30", true);
            extrude(context, id + "F31", {"entities" : qUnion([Q0]), "operationType" : NewBodyOperationType.REMOVE, "oppositeDirection" : true, "depth" : 2 * mm, "offsetDistance" : 25 * mm});
        }
        {
            var Q0;
            Q0=makeQuery(id+"F11.opExtrude","CAP_FACE",FACE,{"disambiguationData":[OSD([sQuery(id+"F10.wireOp",EDGE,"E63.bottom"),sQuery(id+"F10.wireOp",EDGE,"E63.top"),sQuery(id+"F10.wireOp",EDGE,"E63.left"),sQuery(id+"F10.wireOp",EDGE,"E63.right")])],"isStart":false});
            var sketch = newSketch(context, id + "F32", { "sketchPlane" : qUnion([Q0])});
            skCircle(sketch, "E114", {"center": v(-3.87, -19.82) * mm, "radius": 2.5 * mm});
            skSolve(sketch);
        }
        {
            var Q0;
            Q0=makeQuery(id+"F32.imprint","IMPRINT",FACE,{"disambiguationData":[TD([[makeQuery(id+"F32.imprint","IMPRINT",EDGE,{"derivedFrom":sQuery(id+"F32.wireOp",EDGE,"E114")}),1.0]])]});
            extrude(context, id + "F33", {"entities" : qUnion([Q0]), "operationType" : NewBodyOperationType.REMOVE, "oppositeDirection" : true, "depth" : 2 * mm, "offsetDistance" : 25 * mm});
        }
        {
            var Q0;
            Q0=makeQuery(id+"F11.opExtrude","CAP_FACE",FACE,{"disambiguationData":[OSD([sQuery(id+"F10.wireOp",EDGE,"E63.bottom"),sQuery(id+"F10.wireOp",EDGE,"E63.top"),sQuery(id+"F10.wireOp",EDGE,"E63.left"),sQuery(id+"F10.wireOp",EDGE,"E63.right")])],"isStart":false});
            var sketch = newSketch(context, id + "F34", { "sketchPlane" : qUnion([Q0])});
            skCircle(sketch, "E115", {"center": v(-3.87, -10.32) * mm, "radius": 1.5 * mm});
            skSolve(sketch);
        }
        {
            var Q0;
            Q0 = qSketchRegion(id + "F34", true);
            extrude(context, id + "F35", {"entities" : qUnion([Q0]), "operationType" : NewBodyOperationType.REMOVE, "oppositeDirection" : true, "depth" : 2 * mm, "offsetDistance" : 25 * mm});
        }
        {
            var Q0;
            Q0=makeQuery(id+"F11.opExtrude","CAP_FACE",FACE,{"disambiguationData":[OSD([sQuery(id+"F10.wireOp",EDGE,"E63.bottom"),sQuery(id+"F10.wireOp",EDGE,"E63.top"),sQuery(id+"F10.wireOp",EDGE,"E63.left"),sQuery(id+"F10.wireOp",EDGE,"E63.right")])],"isStart":false});
            var sketch = newSketch(context, id + "F36", { "sketchPlane" : qUnion([Q0])});
            skCircle(sketch, "E116", {"center": v(-3.87, -3.82) * mm, "radius": 1.5 * mm});
            skPoint(sketch, "E117", {"position": v(-3.87, -10.32) * mm});
            skSolve(sketch);
        }
        {
            var Q0;
            Q0 = qSketchRegion(id + "F36", true);
            extrude(context, id + "F37", {"entities" : qUnion([Q0]), "operationType" : NewBodyOperationType.REMOVE, "oppositeDirection" : true, "depth" : 2 * mm, "offsetDistance" : 25 * mm});
        }
        {
            var Q0;
            Q0=makeQuery(id+"F11.opExtrude","CAP_FACE",FACE,{"disambiguationData":[OSD([sQuery(id+"F10.wireOp",EDGE,"E63.bottom"),sQuery(id+"F10.wireOp",EDGE,"E63.top"),sQuery(id+"F10.wireOp",EDGE,"E63.left"),sQuery(id+"F10.wireOp",EDGE,"E63.right")])],"isStart":false});
            var sketch = newSketch(context, id + "F38", { "sketchPlane" : qUnion([Q0])});
            skCircle(sketch, "E118", {"center": v(-3.87, 5.68) * mm, "radius": 2.5 * mm});
            skPoint(sketch, "E119", {"position": v(-3.87, -3.82) * mm});
            skSolve(sketch);
        }
        {
            var Q0;
            Q0 = qSketchRegion(id + "F38", true);
            extrude(context, id + "F39", {"entities" : qUnion([Q0]), "operationType" : NewBodyOperationType.REMOVE, "oppositeDirection" : true, "depth" : 2 * mm, "offsetDistance" : 25 * mm});
        }
        {
            var Q0;
            Q0=makeQuery(id+"F7.opExtrude","SWEPT_FACE",FACE,{"disambiguationData":[OSD([sQuery(id+"F6.wireOp",EDGE,"E27")])]});
            var sketch = newSketch(context, id + "F40", { "sketchPlane" : qUnion([Q0])});
            skCircle(sketch, "E120", {"center": v(17.41, 6.88) * mm, "radius": 3.91 * mm});
            skSolve(sketch);
        }
        {
            var Q0;
            Q0 = qSketchRegion(id + "F40", true);
            extrude(context, id + "F41", {"entities" : qUnion([Q0]), "operationType" : NewBodyOperationType.ADD, "oppositeDirection" : true, "depth" : 110.6 * mm, "offsetDistance" : 25 * mm, "hasSecondDirection" : true, "secondDirectionOppositeDirection" : false, "secondDirectionDepth" : 0.6 * mm});
        }
        {
            var Q0;
            Q0=makeQuery(id+"F11.opExtrude","CAP_FACE",FACE,{"disambiguationData":[OSD([sQuery(id+"F10.wireOp",EDGE,"E63.bottom"),sQuery(id+"F10.wireOp",EDGE,"E63.top"),sQuery(id+"F10.wireOp",EDGE,"E63.left"),sQuery(id+"F10.wireOp",EDGE,"E63.right")])],"isStart":false});
            var sketch = newSketch(context, id + "F42", { "sketchPlane" : qUnion([Q0])});
            skLineSegment(sketch, "E121.bottom", {"start": v(-6.7, 73.52) * mm, "end": v(-2.16, 73.52) * mm});
            skLineSegment(sketch, "E121.top", {"start": v(-6.7, -64.37) * mm, "end": v(-2.16, -64.37) * mm});
            skLineSegment(sketch, "E121.left", {"start": v(-6.7, 73.52) * mm, "end": v(-6.7, -64.37) * mm});
            skLineSegment(sketch, "E121.right", {"start": v(-2.16, 73.52) * mm, "end": v(-2.16, -64.37) * mm});
            skSolve(sketch);
        }
        {
            var Q0;
            Q0 = qSketchRegion(id + "F42", true);
            extrude(context, id + "F43", {"entities" : qUnion([Q0]), "operationType" : NewBodyOperationType.ADD, "oppositeDirection" : true, "depth" : 21.8 * mm, "offsetDistance" : 25 * mm, "hasSecondDirection" : true, "secondDirectionOppositeDirection" : false, "secondDirectionDepth" : 0.7 * mm});
        }
    });
